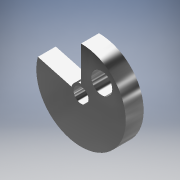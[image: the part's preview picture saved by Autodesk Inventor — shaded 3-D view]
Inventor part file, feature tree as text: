
AUTODESK INVENTOR PART (.ipt)
format: ipt  version: 2018.1 (Build 221171000, 171)  size: 118,272 bytes
history: native  units: in
note: dims shown in document units (in); Inventor stores cm internally (conversion verified against a paired STEP export)
features: extrude x2, sketch x2
ambient origin geometry x8: Origin, YZ Plane, XZ Plane, XY Plane, X Axis, Y Axis, Z Axis, Center Point
bodies: Solid1 (feature_tree)
feature tree (4):
  extrude  "Extrusion1"  Depth=0.1181in TaperAngle=0.0deg
  extrude  "Extrusion2"  [1 undecoded]
  sketch  "Sketch1"  dims[d1=0.1417in d2=0.0in d7=0.1181in d8=0.0in]
  sketch  "Sketch2"
note: 1 required parameter value undecoded (feature->parameter linkage not recoverable at this tier; creation-order binding heuristic only, values carry confidence <= 0.55)
